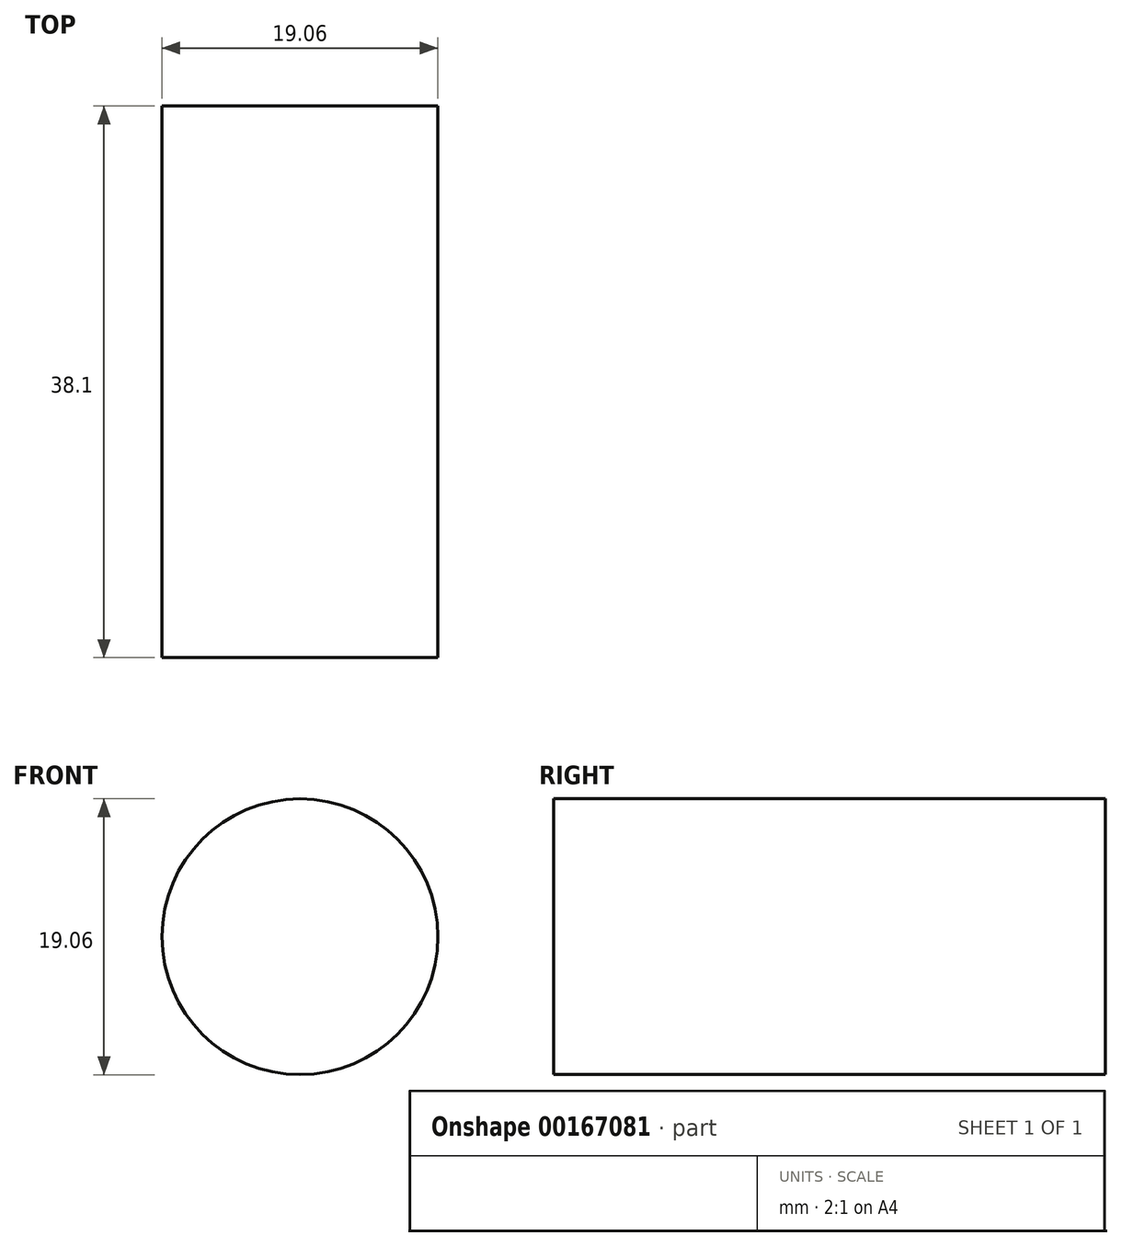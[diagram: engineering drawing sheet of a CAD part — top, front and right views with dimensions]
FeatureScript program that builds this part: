
annotation { "Feature Type Name" : "Feature", "Feature Type Description" : "" }
export const myFeature = defineFeature(function(context is Context, id is Id, definition is map)
    precondition{}
    {
        {
            var Q0;
            Q0=qCreatedBy(makeId("Front.planeOp"),FACE);
            var sketch = newSketch(context, id + "F0", { "sketchPlane" : qUnion([Q0])});
            skCircle(sketch, "E0", {"center": v(0, 0) * mm, "radius": 9.53 * mm});
            skSolve(sketch);
        }
        {
            var Q0;
            Q0 = qSketchRegion(id + "F0", true);
            extrude(context, id + "F1", {"entities" : qUnion([Q0]), "endBound" : BoundingType.SYMMETRIC, "depth" : 38.1 * mm});
        }
    });
